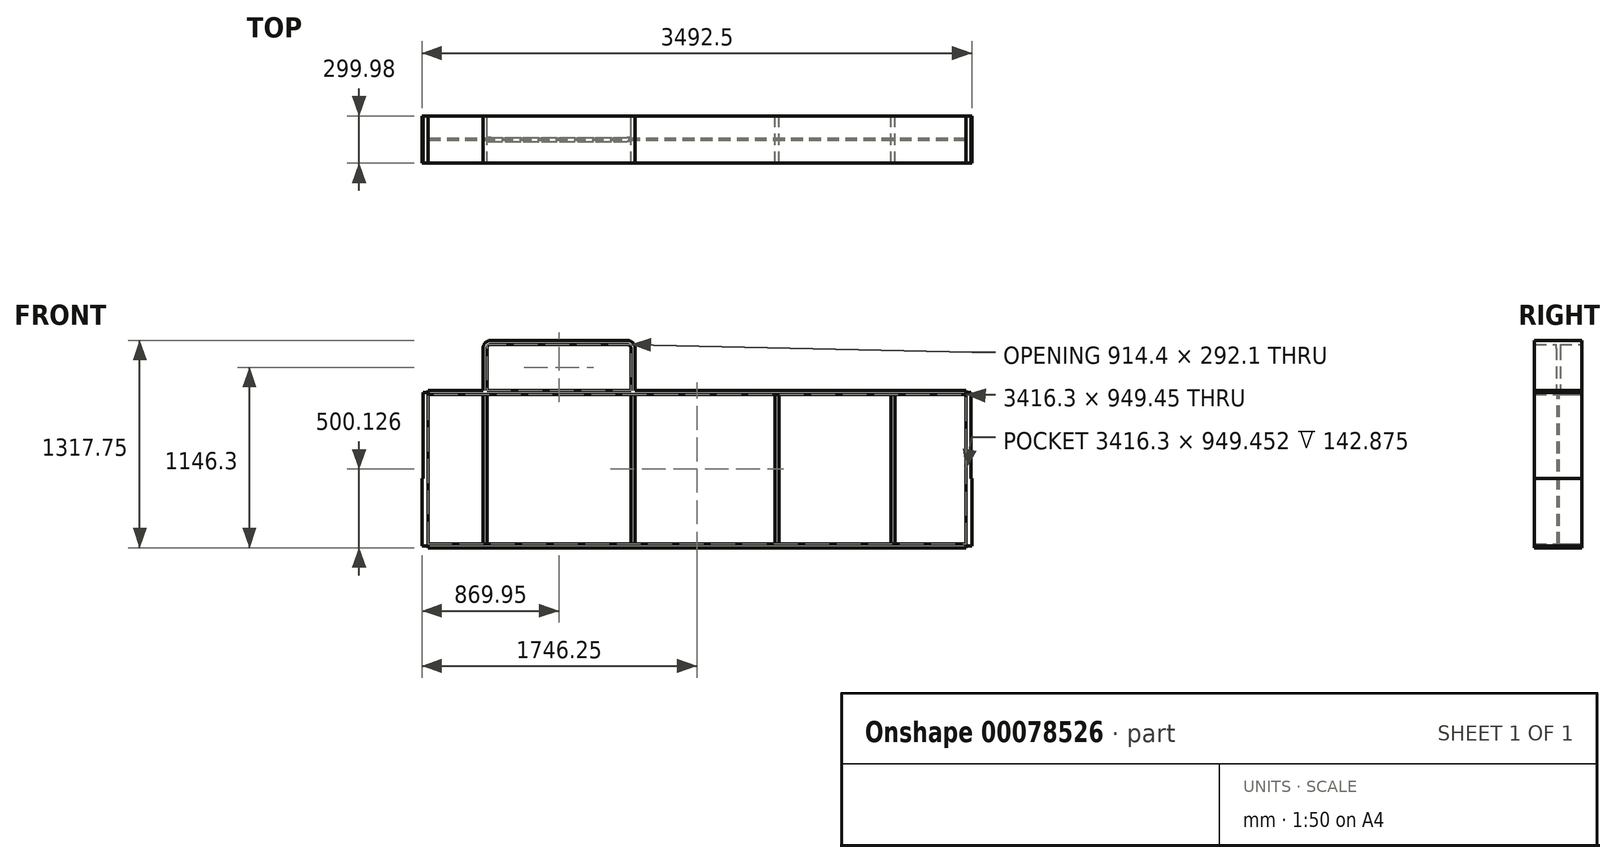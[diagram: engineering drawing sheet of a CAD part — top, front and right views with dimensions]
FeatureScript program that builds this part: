
annotation { "Feature Type Name" : "Feature", "Feature Type Description" : "" }
export const myFeature = defineFeature(function(context is Context, id is Id, definition is map)
    precondition{}
    {
        {
            var Q0;
            Q0=qCreatedBy(makeId("Front.planeOp"),FACE);
            var sketch = newSketch(context, id + "F0", { "sketchPlane" : qUnion([Q0])});
            skLineSegment(sketch, "E0.bottom", {"start": v(-1746.25, 0) * mm, "end": v(1746.25, 0) * mm});
            skLineSegment(sketch, "E0.top", {"start": v(-1746.25, 1000.25) * mm, "end": v(1746.25, 1000.25) * mm});
            skLineSegment(sketch, "E0.left", {"start": v(-1746.25, 0) * mm, "end": v(-1746.25, 1000.25) * mm});
            skLineSegment(sketch, "E0.right", {"start": v(1746.25, 0) * mm, "end": v(1746.25, 1000.25) * mm});
            skSolve(sketch);
        }
        {
            var Q0;
            Q0=qSketchRegion(id+"F0",true);
            extrude(context, id + "F1", {"entities" : qUnion([Q0]), "endBound" : BoundingType.SYMMETRIC, "depth" : 14.22 * mm});
        }
        {
            var Q0;
            Q0=qCreatedBy(makeId("Front.planeOp"),FACE);
            var sketch = newSketch(context, id + "F2", { "sketchPlane" : qUnion([Q0])});
            skLineSegment(sketch, "E1.bottom", {"start": v(-1708.15, 0) * mm, "end": v(1708.15, 0) * mm});
            skLineSegment(sketch, "E1.top", {"start": v(-1708.15, 25.4) * mm, "end": v(1708.15, 25.4) * mm});
            skLineSegment(sketch, "E1.left", {"start": v(-1708.15, 0) * mm, "end": v(-1708.15, 25.4) * mm});
            skLineSegment(sketch, "E1.right", {"start": v(1708.15, 0) * mm, "end": v(1708.15, 25.4) * mm});
            skLineSegment(sketch, "E2.0", {"start": v(1746.25, 0) * mm, "end": v(1746.25, 1000.25) * mm, "construction": true});
            skLineSegment(sketch, "E3.0", {"start": v(-1746.25, 0) * mm, "end": v(-1746.25, 1000.25) * mm, "construction": true});
            skLineSegment(sketch, "E4", {"start": v(-1746.25, 500.13) * mm, "end": v(1746.25, 500.13) * mm, "construction": true});
            skLineSegment(sketch, "E5.MirrorCS", {"start": v(1708.15, 1000.25) * mm, "end": v(1708.15, 974.85) * mm});
            skLineSegment(sketch, "E6.MirrorCS", {"start": v(-1708.15, 1000.25) * mm, "end": v(-1708.15, 974.85) * mm});
            skLineSegment(sketch, "E7.MirrorCS", {"start": v(-1708.15, 974.85) * mm, "end": v(1708.15, 974.85) * mm});
            skLineSegment(sketch, "E8.MirrorCS", {"start": v(-1708.15, 1000.25) * mm, "end": v(1708.15, 1000.25) * mm});
            skPoint(sketch, "E9.oppositeSnap0", {"position": v(-1708.15, 12.7) * mm});
            skLineSegment(sketch, "E9.bottom", {"start": v(-1708.15, 987.55) * mm, "end": v(-1746.25, 987.55) * mm});
            skLineSegment(sketch, "E9.top", {"start": v(-1708.15, 12.7) * mm, "end": v(-1746.25, 12.7) * mm});
            skLineSegment(sketch, "E9.left", {"start": v(-1708.15, 987.55) * mm, "end": v(-1708.15, 12.7) * mm});
            skLineSegment(sketch, "E9.right", {"start": v(-1746.25, 987.55) * mm, "end": v(-1746.25, 12.7) * mm});
            skLineSegment(sketch, "E10", {"start": v(0, 974.85) * mm, "end": v(0, 25.4) * mm, "construction": true});
            skLineSegment(sketch, "E11.MirrorCS", {"start": v(1708.15, 987.55) * mm, "end": v(1746.25, 987.55) * mm});
            skLineSegment(sketch, "E12.MirrorCS", {"start": v(1708.15, 12.7) * mm, "end": v(1746.25, 12.7) * mm});
            skLineSegment(sketch, "E13.MirrorCS", {"start": v(1746.25, 987.55) * mm, "end": v(1746.25, 12.7) * mm});
            skLineSegment(sketch, "E14.MirrorCS", {"start": v(1708.15, 987.55) * mm, "end": v(1708.15, 12.7) * mm});
            skPoint(sketch, "E15.MirrorP", {"position": v(1708.15, 12.7) * mm});
            skSolve(sketch);
        }
        {
            var Q0;
            Q0=qSketchRegion(id+"F2",true);
            extrude(context, id + "F3", {"entities" : qUnion([Q0]), "operationType" : NewBodyOperationType.ADD, "endBound" : BoundingType.SYMMETRIC, "depth" : 299.97 * mm});
        }
        {
            var Q0;
            Q0=qCreatedBy(makeId("Front.planeOp"),FACE);
            var sketch = newSketch(context, id + "F4", { "sketchPlane" : qUnion([Q0])});
            skPoint(sketch, "E16.0", {"position": v(-1746.25, 1000.25) * mm});
            skLineSegment(sketch, "E17.bottom", {"start": v(-1746.25, 1000.25) * mm, "end": v(-1739.9, 1000.25) * mm});
            skLineSegment(sketch, "E17.top", {"start": v(-1746.25, 441.45) * mm, "end": v(-1739.9, 441.45) * mm});
            skLineSegment(sketch, "E17.left", {"start": v(-1746.25, 1000.25) * mm, "end": v(-1746.25, 441.45) * mm});
            skLineSegment(sketch, "E17.right", {"start": v(-1739.9, 1000.25) * mm, "end": v(-1739.9, 441.45) * mm});
            skLineSegment(sketch, "E18", {"start": v(0, -58.3) * mm, "end": v(0, 1155.28) * mm, "construction": true});
            skLineSegment(sketch, "E19.MirrorCS", {"start": v(1746.25, 1000.25) * mm, "end": v(1739.9, 1000.25) * mm});
            skLineSegment(sketch, "E20.MirrorCS", {"start": v(1746.25, 441.45) * mm, "end": v(1739.9, 441.45) * mm});
            skPoint(sketch, "E21.MirrorP", {"position": v(1746.25, 1000.25) * mm});
            skLineSegment(sketch, "E22.MirrorCS", {"start": v(1739.9, 1000.25) * mm, "end": v(1739.9, 441.45) * mm});
            skLineSegment(sketch, "E23.MirrorCS", {"start": v(1746.25, 1000.25) * mm, "end": v(1746.25, 441.45) * mm});
            skSolve(sketch);
        }
        {
            var Q0;
            Q0=qSketchRegion(id+"F4",true);
            extrude(context, id + "F5", {"entities" : qUnion([Q0]), "operationType" : NewBodyOperationType.REMOVE, "endBound" : BoundingType.SYMMETRIC, "oppositeDirection" : true, "depth" : 304.8 * mm});
        }
        {
            var Q0;
            Q0=makeQuery(id+"F3.opExtrude","CAP_FACE",FACE,{"disambiguationData":[OSD([sQuery(id+"F2.wireOp",EDGE,"E1.bottom"),sQuery(id+"F2.wireOp",EDGE,"E1.top"),sQuery(id+"F2.wireOp",EDGE,"E1.left"),sQuery(id+"F2.wireOp",EDGE,"E6.MirrorCS"),sQuery(id+"F2.wireOp",EDGE,"E7.MirrorCS"),sQuery(id+"F2.wireOp",EDGE,"E8.MirrorCS"),sQuery(id+"F2.wireOp",EDGE,"E9.bottom"),sQuery(id+"F2.wireOp",EDGE,"E9.top"),sQuery(id+"F2.wireOp",EDGE,"E9.left"),sQuery(id+"F2.wireOp",EDGE,"E9.right"),sQuery(id+"F2.wireOp",EDGE,"E5.MirrorCS"),sQuery(id+"F2.wireOp",EDGE,"E1.right"),sQuery(id+"F2.wireOp",EDGE,"E11.MirrorCS"),sQuery(id+"F2.wireOp",EDGE,"E12.MirrorCS"),sQuery(id+"F2.wireOp",EDGE,"E13.MirrorCS"),sQuery(id+"F2.wireOp",EDGE,"E14.MirrorCS")])],"isStart":false});
            var sketch = newSketch(context, id + "F6", { "sketchPlane" : qUnion([Q0])});
            skLineSegment(sketch, "E24.bottom", {"start": v(-1708.15, 987.55) * mm, "end": v(-1777.82, 987.55) * mm});
            skLineSegment(sketch, "E24.top", {"start": v(-1708.15, 1019.74) * mm, "end": v(-1777.82, 1019.74) * mm});
            skLineSegment(sketch, "E24.left", {"start": v(-1708.15, 987.55) * mm, "end": v(-1708.15, 1019.74) * mm});
            skLineSegment(sketch, "E24.right", {"start": v(-1777.82, 987.55) * mm, "end": v(-1777.82, 1019.74) * mm});
            skLineSegment(sketch, "E25.bottom", {"start": v(1708.15, 987.55) * mm, "end": v(1769.2, 987.55) * mm});
            skLineSegment(sketch, "E25.top", {"start": v(1708.15, 1033.96) * mm, "end": v(1769.2, 1033.96) * mm});
            skLineSegment(sketch, "E25.left", {"start": v(1708.15, 987.55) * mm, "end": v(1708.15, 1033.96) * mm});
            skLineSegment(sketch, "E25.right", {"start": v(1769.2, 987.55) * mm, "end": v(1769.2, 1033.96) * mm});
            skLineSegment(sketch, "E26.bottom", {"start": v(1708.15, 12.7) * mm, "end": v(1775.25, 12.7) * mm});
            skLineSegment(sketch, "E26.top", {"start": v(1708.15, -29.13) * mm, "end": v(1775.25, -29.13) * mm});
            skLineSegment(sketch, "E26.left", {"start": v(1708.15, 12.7) * mm, "end": v(1708.15, -29.13) * mm});
            skLineSegment(sketch, "E26.right", {"start": v(1775.25, 12.7) * mm, "end": v(1775.25, -29.13) * mm});
            skLineSegment(sketch, "E27.bottom", {"start": v(-1708.15, 12.7) * mm, "end": v(-1780.9, 12.7) * mm});
            skLineSegment(sketch, "E27.top", {"start": v(-1708.15, -36.57) * mm, "end": v(-1780.9, -36.57) * mm});
            skLineSegment(sketch, "E27.left", {"start": v(-1708.15, 12.7) * mm, "end": v(-1708.15, -36.57) * mm});
            skLineSegment(sketch, "E27.right", {"start": v(-1780.9, 12.7) * mm, "end": v(-1780.9, -36.57) * mm});
            skSolve(sketch);
        }
        {
            var Q0;
            Q0=qSketchRegion(id+"F6",true);
            extrude(context, id + "F7", {"entities" : qUnion([Q0]), "operationType" : NewBodyOperationType.REMOVE, "endBound" : BoundingType.THROUGH_ALL, "oppositeDirection" : true, "depth" : 25.4 * mm});
        }
        {
            var Q0;
            Q0=qCreatedBy(makeId("Front.planeOp"),FACE);
            var sketch = newSketch(context, id + "F8", { "sketchPlane" : qUnion([Q0])});
            skLineSegment(sketch, "E28.0", {"start": v(-876.3, 987.55) * mm, "end": v(-876.3, 441.45) * mm, "construction": true});
            skLineSegment(sketch, "E29.0", {"start": v(876.3, 987.55) * mm, "end": v(876.3, 441.45) * mm, "construction": true});
            skLineSegment(sketch, "E30.0", {"start": v(-1708.15, 25.4) * mm, "end": v(1708.15, 25.4) * mm});
            skLineSegment(sketch, "E31.0", {"start": v(-1333.5, 1317.75) * mm, "end": v(-1333.5, 25.4) * mm});
            skLineSegment(sketch, "E32.0", {"start": v(-1358.9, 1266.95) * mm, "end": v(-1358.9, 25.4) * mm});
            skLineSegment(sketch, "E33.0", {"start": v(-1308.1, 1317.75) * mm, "end": v(-444.5, 1317.75) * mm});
            skLineSegment(sketch, "E34.0", {"start": v(-1308.1, 1292.35) * mm, "end": v(-444.5, 1292.35) * mm});
            skLineSegment(sketch, "E34.1", {"start": v(-1333.5, 1266.95) * mm, "end": v(-1333.5, 25.4) * mm});
            skLineSegment(sketch, "E35.MirrorCS", {"start": v(-419.1, 1266.95) * mm, "end": v(-419.1, 25.4) * mm});
            skLineSegment(sketch, "E36.MirrorCS", {"start": v(-393.7, 1266.95) * mm, "end": v(-393.7, 25.4) * mm});
            skLineSegment(sketch, "E37.MirrorCS", {"start": v(-419.1, 1292.35) * mm, "end": v(-419.1, 25.4) * mm});
            skPoint(sketch, "E38.visualSharp", {"position": v(-1333.5, 1292.35) * mm});
            skArc(sketch, "E38.filletArc", {"start": v(-1308.1, 1292.35) * mm, "mid": v(-1326.06, 1284.91) * mm, "end": v(-1333.5, 1266.95) * mm});
            skPoint(sketch, "E39.newPointB", {"position": v(-419.1, 1317.75) * mm});
            skArc(sketch, "E39.filletArc", {"start": v(-419.1, 1266.95) * mm, "mid": v(-426.54, 1284.91) * mm, "end": v(-444.5, 1292.35) * mm});
            skPoint(sketch, "E40.visualSharp", {"position": v(-1358.9, 1317.75) * mm});
            skArc(sketch, "E40.filletArc", {"start": v(-1308.1, 1317.75) * mm, "mid": v(-1344.02, 1302.87) * mm, "end": v(-1358.9, 1266.95) * mm});
            skPoint(sketch, "E41.visualSharp", {"position": v(-393.7, 1317.75) * mm});
            skArc(sketch, "E41.filletArc", {"start": v(-393.7, 1266.95) * mm, "mid": v(-408.58, 1302.87) * mm, "end": v(-444.5, 1317.75) * mm});
            skLineSegment(sketch, "E42", {"start": v(0, 1077.49) * mm, "end": v(0, -160.54) * mm, "construction": true});
            skLineSegment(sketch, "E43.0", {"start": v(-1708.15, 974.85) * mm, "end": v(1708.15, 974.85) * mm});
            skLineSegment(sketch, "E44.0.1", {"start": v(1708.15, 25.4) * mm, "end": v(1708.15, 974.85) * mm});
            skLineSegment(sketch, "E44.0.2", {"start": v(1708.15, 974.85) * mm, "end": v(-1708.15, 974.85) * mm});
            skLineSegment(sketch, "E44.0.3", {"start": v(-1708.15, 974.85) * mm, "end": v(-1708.15, 25.4) * mm});
            skLineSegment(sketch, "E45.0", {"start": v(520.7, 974.85) * mm, "end": v(520.7, 25.4) * mm});
            skLineSegment(sketch, "E46.0", {"start": v(495.3, 974.85) * mm, "end": v(495.3, 25.4) * mm});
            skLineSegment(sketch, "E47.MirrorCS", {"start": v(1231.9, 974.85) * mm, "end": v(1231.9, 25.4) * mm});
            skLineSegment(sketch, "E48.MirrorCS", {"start": v(1257.3, 974.85) * mm, "end": v(1257.3, 25.4) * mm});
            skSolve(sketch);
        }
        {
            var Q0;
            Q0=makeQuery(id+"F8.imprint","IMPRINT",FACE,{"disambiguationData":[TD([[makeQuery(id+"F8.imprint","IMPRINT",EDGE,{"derivedFrom":sQuery(id+"F8.wireOp",EDGE,"E34.0")}),-1.0]])]});
            extrude(context, id + "F9", {"entities" : qUnion([Q0]), "operationType" : NewBodyOperationType.ADD, "endBound" : BoundingType.SYMMETRIC, "depth" : 25.4 * mm});
        }
        {
            var Q0;
            {var subQ0=sQuery(id+"F8.wireOp",EDGE,"E40.filletArc");var subQ1=sQuery(id+"F8.wireOp",EDGE,"E32.0");var subQ2=makeQuery(id+"F8.imprint","INTERSECT",VERTEX,{"derivedFrom":[subQ1,subQ0]});Q0=makeQuery(id+"F8.imprint","IMPRINT",FACE,{"disambiguationData":[TD([[makeQuery(id+"F8.imprint","IMPRINT",EDGE,{"disambiguationData":[TD([[subQ2,-1.0]])],"derivedFrom":subQ1}),1.0]])]});}
            var Q1;
            {var subQ7=sQuery(id+"F8.wireOp",EDGE,"E33.0");Q1=makeQuery(id+"F8.imprint","IMPRINT",FACE,{"disambiguationData":[TD([[makeQuery(id+"F8.imprint","IMPRINT",EDGE,{"derivedFrom":subQ7}),-1.0]])]});}
            extrude(context, id + "F10", {"entities" : qUnion([Q0, Q1]), "operationType" : NewBodyOperationType.ADD, "endBound" : BoundingType.SYMMETRIC, "depth" : 299.97 * mm});
        }
        {
            var Q0;
            {var subQ0=sQuery(id+"F8.wireOp",EDGE,"E30.0");var subQ1=sQuery(id+"F8.wireOp",EDGE,"E32.0");var subQ2=makeQuery(id+"F8.imprint","INTERSECT",VERTEX,{"derivedFrom":[subQ1,subQ0]});Q0=makeQuery(id+"F8.imprint","IMPRINT",FACE,{"disambiguationData":[TD([[makeQuery(id+"F8.imprint","IMPRINT",EDGE,{"disambiguationData":[TD([[subQ2,1.0]])],"derivedFrom":subQ1}),1.0]])]});}
            var Q1;
            {var subQ0=sQuery(id+"F8.wireOp",EDGE,"E30.0");var subQ1=sQuery(id+"F8.wireOp",EDGE,"E36.MirrorCS");var subQ2=makeQuery(id+"F8.imprint","INTERSECT",VERTEX,{"derivedFrom":[subQ1,subQ0]});Q1=makeQuery(id+"F8.imprint","IMPRINT",FACE,{"disambiguationData":[TD([[makeQuery(id+"F8.imprint","IMPRINT",EDGE,{"disambiguationData":[TD([[subQ2,1.0]])],"derivedFrom":subQ1}),-1.0]])]});}
            var Q2;
            {var subQ0=sQuery(id+"F8.wireOp",EDGE,"E45.0");Q2=makeQuery(id+"F8.imprint","IMPRINT",FACE,{"disambiguationData":[TD([[makeQuery(id+"F8.imprint","IMPRINT",EDGE,{"derivedFrom":subQ0}),-1.0]])]});}
            var Q3;
            {var subQ0=sQuery(id+"F8.wireOp",EDGE,"E47.MirrorCS");Q3=makeQuery(id+"F8.imprint","IMPRINT",FACE,{"disambiguationData":[TD([[makeQuery(id+"F8.imprint","IMPRINT",EDGE,{"derivedFrom":subQ0}),1.0]])]});}
            extrude(context, id + "F11", {"entities" : qUnion([Q0, Q1, Q2, Q3]), "endBound" : BoundingType.SYMMETRIC, "depth" : 299.97 * mm});
        }
    });
